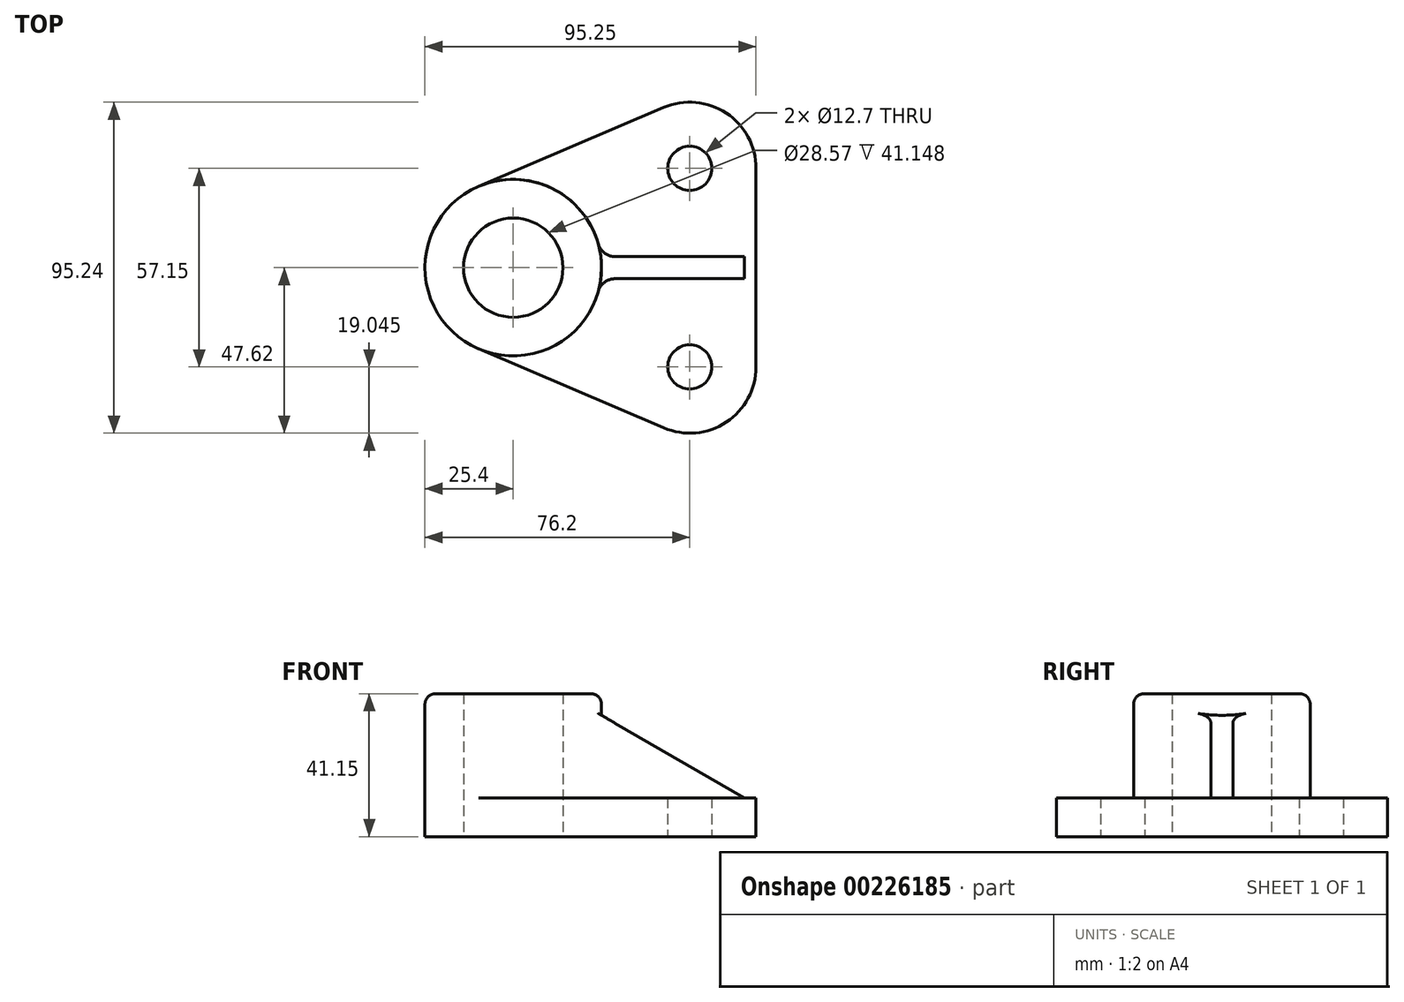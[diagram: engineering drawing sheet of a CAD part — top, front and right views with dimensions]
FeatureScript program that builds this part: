
annotation { "Feature Type Name" : "Feature", "Feature Type Description" : "" }
export const myFeature = defineFeature(function(context is Context, id is Id, definition is map)
    precondition{}
    {
        {
            var Q0;
            Q0=qCreatedBy(makeId("Top.planeOp"),FACE);
            var sketch = newSketch(context, id + "F0", { "sketchPlane" : qUnion([Q0])});
            skCircle(sketch, "E0", {"center": v(0, 0) * mm, "radius": 25.4 * mm});
            skCircle(sketch, "E1", {"center": v(0, 0) * mm, "radius": 14.29 * mm});
            skSolve(sketch);
        }
        {
            var Q0;
            Q0=qCreatedBy(makeId("Top.planeOp"),FACE);
            var sketch = newSketch(context, id + "F1", { "sketchPlane" : qUnion([Q0])});
            skCircle(sketch, "E2", {"center": v(50.8, 28.58) * mm, "radius": 6.35 * mm});
            skCircle(sketch, "E3", {"center": v(50.8, -28.58) * mm, "radius": 6.35 * mm});
            skLineSegment(sketch, "E4", {"start": v(43.33, 46.1) * mm, "end": v(-9.97, 23.36) * mm});
            skCircle(sketch, "E5.0", {"center": v(0, 0) * mm, "radius": 25.4 * mm});
            skArc(sketch, "E6", {"start": v(43.33, -46.1) * mm, "mid": v(61.3, -44.47) * mm, "end": v(69.85, -28.58) * mm});
            skArc(sketch, "E7", {"start": v(43.33, 46.1) * mm, "mid": v(61.3, 44.47) * mm, "end": v(69.85, 28.58) * mm});
            skLineSegment(sketch, "E8", {"start": v(69.85, 28.58) * mm, "end": v(69.85, -28.58) * mm});
            skLineSegment(sketch, "E9", {"start": v(-9.97, -23.36) * mm, "end": v(43.33, -46.1) * mm});
            skSolve(sketch);
        }
        {
            var Q0;
            Q0=makeQuery(id+"F0.imprint","IMPRINT",FACE,{"disambiguationData":[TD([[makeQuery(id+"F0.imprint","IMPRINT",EDGE,{"derivedFrom":sQuery(id+"F0.wireOp",EDGE,"E0")}),1.0]])]});
            extrude(context, id + "F2", {"entities" : qUnion([Q0]), "depth" : 41.15 * mm});
        }
        {
            var Q0;
            Q0=makeQuery(id+"F1.imprint","IMPRINT",FACE,{"disambiguationData":[TD([[makeQuery(id+"F1.imprint","IMPRINT",EDGE,{"derivedFrom":sQuery(id+"F1.wireOp",EDGE,"E2")}),-1.0]])]});
            extrude(context, id + "F3", {"entities" : qUnion([Q0]), "operationType" : NewBodyOperationType.ADD, "depth" : 11.18 * mm});
        }
        {
            var Q0;
            Q0=makeQuery(id+"F2.opExtrude","CAP_EDGE",EDGE,{"disambiguationData":[OSD([sQuery(id+"F0.wireOp",EDGE,"E0")])],"isStart":false});
            fillet(context, id + "F4", {"entities" : qUnion([Q0]), "radius" : 3.05 * mm, "tangentPropagation" : true, "allowEdgeOverflow" : false});
        }
        {
            var Q0;
            Q0=qCreatedBy(makeId("Front.planeOp"),FACE);
            var sketch = newSketch(context, id + "F5", { "sketchPlane" : qUnion([Q0])});
            skLineSegment(sketch, "E10", {"start": v(19.91, 38.1) * mm, "end": v(66.55, 11.18) * mm});
            skLineSegment(sketch, "E11.0.0", {"start": v(43.33, 11.18) * mm, "end": v(-9.97, 11.18) * mm});
            skLineSegment(sketch, "E11.0.1", {"start": v(-9.97, 11.18) * mm, "end": v(25.4, 11.18) * mm});
            skLineSegment(sketch, "E11.0.2", {"start": v(-9.97, 11.18) * mm, "end": v(43.33, 11.18) * mm});
            skLineSegment(sketch, "E11.0.3", {"start": v(43.33, 11.18) * mm, "end": v(69.85, 11.18) * mm});
            skLineSegment(sketch, "E11.0.5", {"start": v(69.85, 11.18) * mm, "end": v(43.33, 11.18) * mm});
            skLineSegment(sketch, "E12.0.0", {"start": v(43.33, 0) * mm, "end": v(69.85, 0) * mm});
            skLineSegment(sketch, "E12.0.1", {"start": v(69.85, 0) * mm, "end": v(69.85, 11.18) * mm});
            skLineSegment(sketch, "E12.0.3", {"start": v(43.33, 11.18) * mm, "end": v(43.33, 0) * mm});
            skLineSegment(sketch, "E13.0", {"start": v(25.4, 38.1) * mm, "end": v(-25.4, 38.1) * mm});
            skLineSegment(sketch, "E14", {"start": v(19.91, 38.1) * mm, "end": v(19.91, 11.18) * mm});
            skSolve(sketch);
        }
        {
            var Q0;
            {var subQ0=sQuery(id+"F5.wireOp",EDGE,"E10");Q0=makeQuery(id+"F5.imprint","IMPRINT",FACE,{"disambiguationData":[TD([[makeQuery(id+"F5.imprint","IMPRINT",EDGE,{"derivedFrom":subQ0}),-1.0]])]});}
            extrude(context, id + "F6", {"entities" : qUnion([Q0]), "operationType" : NewBodyOperationType.ADD, "endBound" : BoundingType.SYMMETRIC, "depth" : 6.35 * mm});
        }
        {
            var Q0;
            Q0=makeQuery(id+"F6.boolean.opBoolean","INTERSECT",EDGE,{"derivedFrom":[makeQuery(id+"F2.opExtrude","SWEPT_FACE",FACE,{"disambiguationData":[OSD([sQuery(id+"F0.wireOp",EDGE,"E0")])]}),makeQuery(id+"F6.opExtrude","CAP_FACE",FACE,{"disambiguationData":[OSD([sQuery(id+"F5.wireOp",EDGE,"E10"),sQuery(id+"F5.wireOp",EDGE,"E11.0.2"),sQuery(id+"F5.wireOp",EDGE,"E11.0.5"),sQuery(id+"F5.wireOp",EDGE,"E14")])],"isStart":false})]});
            var Q1;
            Q1=makeQuery(id+"F6.opExtrude","CAP_EDGE",EDGE,{"disambiguationData":[OSD([sQuery(id+"F5.wireOp",EDGE,"E11.0.2"),sQuery(id+"F5.wireOp",EDGE,"E11.0.5")])],"isStart":false});
            var Q2;
            {var subQ0=sQuery(id+"F1.wireOp",EDGE,"E9");var subQ1=sQuery(id+"F1.wireOp",EDGE,"E5.0");Q2=makeQuery(id+"F6.boolean.opBoolean","SPLIT",EDGE,{"disambiguationData":[TD([makeQuery(id+"F3.opExtrude","SWEPT_FACE",FACE,{"disambiguationData":[OSD([subQ0])]})])],"derivedFrom":makeQuery(id+"F3.opExtrude","CAP_EDGE",EDGE,{"disambiguationData":[OSD([subQ1])],"isStart":false})});}
            var Q3;
            {var subQ0=sQuery(id+"F1.wireOp",EDGE,"E5.0");var subQ1=sQuery(id+"F1.wireOp",EDGE,"E4");Q3=makeQuery(id+"F6.boolean.opBoolean","SPLIT",EDGE,{"disambiguationData":[TD([makeQuery(id+"F3.opExtrude","SWEPT_FACE",FACE,{"disambiguationData":[OSD([subQ1])]})])],"derivedFrom":makeQuery(id+"F3.opExtrude","CAP_EDGE",EDGE,{"disambiguationData":[OSD([subQ0])],"isStart":false})});}
            var Q4;
            Q4=makeQuery(id+"F6.opExtrude","CAP_EDGE",EDGE,{"disambiguationData":[OSD([sQuery(id+"F5.wireOp",EDGE,"E11.0.2"),sQuery(id+"F5.wireOp",EDGE,"E11.0.5")])],"isStart":true});
            var Q5;
            Q5=makeQuery(id+"F6.boolean.opBoolean","INTERSECT",EDGE,{"derivedFrom":[makeQuery(id+"F2.opExtrude","SWEPT_FACE",FACE,{"disambiguationData":[OSD([sQuery(id+"F0.wireOp",EDGE,"E0")])]}),makeQuery(id+"F6.opExtrude","CAP_FACE",FACE,{"disambiguationData":[OSD([sQuery(id+"F5.wireOp",EDGE,"E10"),sQuery(id+"F5.wireOp",EDGE,"E11.0.2"),sQuery(id+"F5.wireOp",EDGE,"E11.0.5"),sQuery(id+"F5.wireOp",EDGE,"E14")])],"isStart":true})]});
            fillet(context, id + "F7", {"entities" : qUnion([Q0, Q1, Q2, Q3, Q4, Q5]), "radius" : 5.08 * mm, "tangentPropagation" : true, "allowEdgeOverflow" : false});
        }
    });
